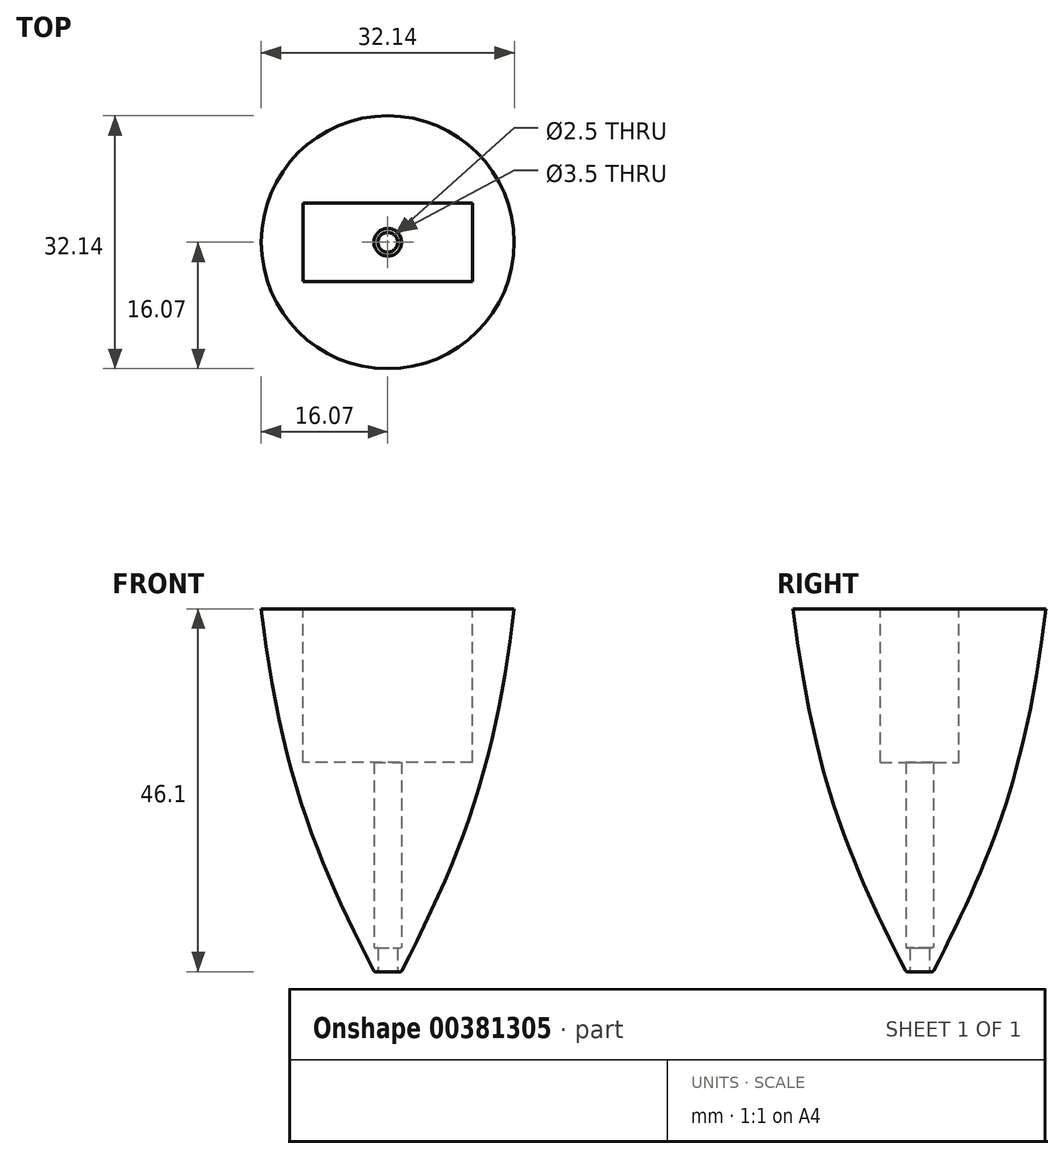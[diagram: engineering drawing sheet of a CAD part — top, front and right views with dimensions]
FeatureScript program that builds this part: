
annotation { "Feature Type Name" : "Feature", "Feature Type Description" : "" }
export const myFeature = defineFeature(function(context is Context, id is Id, definition is map)
    precondition{}
    {
        {
            var Q0;
            Q0=qCreatedBy(makeId("Front.planeOp"),FACE);
            var sketch = newSketch(context, id + "F0", { "sketchPlane" : qUnion([Q0])});
            skLineSegment(sketch, "E0.bottom", {"start": v(10.75, -19.5) * mm, "end": v(-10.75, -19.5) * mm});
            skLineSegment(sketch, "E0.top", {"start": v(10.75, 44.5) * mm, "end": v(9, 44.5) * mm});
            skLineSegment(sketch, "E0.left", {"start": v(10.75, -19.5) * mm, "end": v(10.75, 44.5) * mm});
            skLineSegment(sketch, "E0.right", {"start": v(-10.75, -19.5) * mm, "end": v(-10.75, 44.5) * mm});
            skPoint(sketch, "E0.middle", {"position": v(0, 12.5) * mm});
            skLineSegment(sketch, "E1", {"start": v(-10.75, 0) * mm, "end": v(10.75, 0) * mm, "construction": true});
            skLineSegment(sketch, "E2.top", {"start": v(9, 50.5) * mm, "end": v(-9, 50.5) * mm});
            skLineSegment(sketch, "E2.left", {"start": v(9, 44.5) * mm, "end": v(9, 50.5) * mm});
            skLineSegment(sketch, "E2.right", {"start": v(-9, 44.5) * mm, "end": v(-9, 50.5) * mm});
            skPoint(sketch, "E2.middle", {"position": v(0, 47.5) * mm});
            skPoint(sketch, "E2.middle.positionSnap0", {"position": v(0, 44.5) * mm});
            skPoint(sketch, "E2.centerSnap0", {"position": v(0, 44.5) * mm});
            skLineSegment(sketch, "E3.trimOffspring", {"start": v(-9, 44.5) * mm, "end": v(-10.75, 44.5) * mm});
            skSolve(sketch);
        }
        {
            var Q0;
            Q0=qCreatedBy(makeId("Front.planeOp"),FACE);
            var sketch = newSketch(context, id + "F1", { "sketchPlane" : qUnion([Q0])});
            skLineSegment(sketch, "E4", {"start": v(0, 0) * mm, "end": v(0, 25) * mm, "construction": true});
            skLineSegment(sketch, "E5", {"start": v(-17.5, 25) * mm, "end": v(17.5, 25) * mm, "construction": true});
            skLineSegment(sketch, "E6", {"start": v(-15, 47) * mm, "end": v(-2, 47) * mm, "construction": true});
            skPoint(sketch, "E7", {"position": v(0, 47) * mm});
            skPoint(sketch, "E8", {"position": v(0, -19.5) * mm});
            skLineSegment(sketch, "E9", {"start": v(-12.5, -19.5) * mm, "end": v(-1.25, -19.5) * mm, "construction": true});
            skLineSegment(sketch, "E10", {"start": v(0, -19.5) * mm, "end": v(0, -49.5) * mm, "construction": true});
            skLineSegment(sketch, "E11", {"start": v(0, 47) * mm, "end": v(0, 62) * mm, "construction": true});
            skLineSegment(sketch, "E12", {"start": v(-10, 62) * mm, "end": v(-2, 62) * mm});
            skFitSpline(sketch, "E13", {"points": [v(-10, 62) * mm, v(-15, 47) * mm, v(-17.5, 25) * mm, v(-12.5, -19.5) * mm, v(0, -49.5) * mm], "startDerivative": vector(-28.9, -76.62) * mm, "endDerivative": vector(51.56, -101.04) * mm});
            skLineSegment(sketch, "E14.0", {"start": v(-2, 50) * mm, "end": v(-2, 62) * mm});
            skPoint(sketch, "E15.orphan", {"position": v(10, 62) * mm});
            skLineSegment(sketch, "E16.0", {"start": v(-1.25, -43.05) * mm, "end": v(-1.25, -47.05) * mm});
            skLineSegment(sketch, "E17", {"start": v(0, 47) * mm, "end": v(-2, 47) * mm});
            skLineSegment(sketch, "E18", {"start": v(0, 50) * mm, "end": v(-2, 50) * mm});
            skLineSegment(sketch, "E19.trimOffspring", {"start": v(0, 47) * mm, "end": v(15, 47) * mm, "construction": true});
            skLineSegment(sketch, "E20.trimOffspring", {"start": v(0, -19.5) * mm, "end": v(12.5, -19.5) * mm, "construction": true});
            skLineSegment(sketch, "E21", {"start": v(0, 50) * mm, "end": v(0, -19.5) * mm});
            skLineSegment(sketch, "E22", {"start": v(0, -19.5) * mm, "end": v(-1.75, -19.5) * mm});
            skLineSegment(sketch, "E23", {"start": v(-1.75, -19.5) * mm, "end": v(-1.75, -43.05) * mm});
            skLineSegment(sketch, "E24", {"start": v(-1.25, -43.05) * mm, "end": v(-1.75, -43.05) * mm});
            skSolve(sketch);
        }
        {
            var Q0;
            Q0=makeQuery(id+"F1.imprint","IMPRINT",FACE,{"disambiguationData":[TD([[makeQuery(id+"F1.imprint","IMPRINT",EDGE,{"derivedFrom":sQuery(id+"F1.wireOp",EDGE,"E12")}),-1.0]])]});
            var Q1;
            Q1=sQuery(id+"F1.wireOp",EDGE,"E11");
            revolve(context, id + "F2", {"entities" : qUnion([Q0]), "axis" : qUnion([Q1]), "revolveType" : RevolveType.FULL});
        }
        {
            var Q0;
            Q0=qSketchRegion(id+"F0",true);
            extrude(context, id + "F3", {"entities" : qUnion([Q0]), "operationType" : NewBodyOperationType.REMOVE, "endBound" : BoundingType.SYMMETRIC, "depth" : 10 * mm});
        }
        {
            var Q0;
            Q0=makeQuery(id+"F2.opRevolve","SWEPT_FACE",FACE,{"disambiguationData":[OSD([sQuery(id+"F1.wireOp",EDGE,"E12")])]});
            var sketch = newSketch(context, id + "F4", { "sketchPlane" : qUnion([Q0])});
            skCircle(sketch, "E25.cCircle", {"center": v(0, 0) * mm, "radius": 2 * mm, "construction": true});
            skLineSegment(sketch, "E25.0", {"start": v(2.3, 0.1) * mm, "end": v(1.24, -1.95) * mm});
            skLineSegment(sketch, "E25.1", {"start": v(1.24, -1.95) * mm, "end": v(-1.06, -2.05) * mm});
            skLineSegment(sketch, "E25.2", {"start": v(-1.06, -2.05) * mm, "end": v(-2.3, -0.1) * mm});
            skLineSegment(sketch, "E25.3", {"start": v(-2.3, -0.1) * mm, "end": v(-1.24, 1.95) * mm});
            skLineSegment(sketch, "E25.4", {"start": v(-1.24, 1.95) * mm, "end": v(1.06, 2.05) * mm});
            skLineSegment(sketch, "E25.5", {"start": v(1.06, 2.05) * mm, "end": v(2.3, 0.1) * mm});
            skPoint(sketch, "E25.0.midPoint", {"position": v(1.77, -0.92) * mm});
            skSolve(sketch);
        }
        {
            var Q0;
            Q0=qSketchRegion(id+"F4",true);
            extrude(context, id + "F5", {"entities" : qUnion([Q0]), "operationType" : NewBodyOperationType.REMOVE, "oppositeDirection" : true, "depth" : 15 * mm});
        }
        {
            var Q0;
            Q0=qCreatedBy(makeId("Right.planeOp"),FACE);
            var sketch = newSketch(context, id + "F6", { "sketchPlane" : qUnion([Q0])});
            skLineSegment(sketch, "E26.bottom", {"start": v(0.1, 47) * mm, "end": v(-1.9, 47) * mm});
            skLineSegment(sketch, "E26.top", {"start": v(0.1, 50) * mm, "end": v(-1.9, 50) * mm});
            skLineSegment(sketch, "E26.left", {"start": v(0.1, 47) * mm, "end": v(0.1, 50) * mm});
            skLineSegment(sketch, "E26.right", {"start": v(-1.9, 47) * mm, "end": v(-1.9, 50) * mm});
            skPoint(sketch, "E26.middle", {"position": v(0, 48) * mm});
            skSolve(sketch);
        }
        {
            var Q0;
            Q0=qSketchRegion(id+"F6",true);
            extrude(context, id + "F7", {"entities" : qUnion([Q0]), "operationType" : NewBodyOperationType.REMOVE, "endBound" : BoundingType.SYMMETRIC, "oppositeDirection" : true, "depth" : 41 * mm});
        }
        {
            var Q0;
            Q0=qCreatedBy(makeId("Front.planeOp"),FACE);
            var sketch = newSketch(context, id + "F8", { "sketchPlane" : qUnion([Q0])});
            skLineSegment(sketch, "E27.bottom", {"start": v(1.5, 41) * mm, "end": v(-1.5, 41) * mm});
            skLineSegment(sketch, "E27.top", {"start": v(1.5, 42) * mm, "end": v(-1.5, 42) * mm});
            skLineSegment(sketch, "E27.left", {"start": v(1.5, 41) * mm, "end": v(1.5, 42) * mm});
            skLineSegment(sketch, "E27.right", {"start": v(-1.5, 41) * mm, "end": v(-1.5, 42) * mm});
            skPoint(sketch, "E27.middle", {"position": v(0, 41.5) * mm});
            skSolve(sketch);
        }
        {
            var Q0;
            Q0=qSketchRegion(id+"F8",true);
            extrude(context, id + "F9", {"entities" : qUnion([Q0]), "operationType" : NewBodyOperationType.REMOVE, "endBound" : BoundingType.THROUGH_ALL, "depth" : 25 * mm});
        }
        {
            var Q0;
            Q0=makeQuery(id+"F2.opRevolve","SWEPT_EDGE",EDGE,{"disambiguationData":[OSD([sQuery(id+"F1.wireOp",EDGE,"E13"),sQuery(id+"F1.wireOp",EDGE,"E16.0")])]});
            fillet(context, id + "F10", {"entities" : qUnion([Q0]), "radius" : 0.3 * mm, "tangentPropagation" : true, "allowEdgeOverflow" : false});
        }
        {
            var Q0;
            Q0=makeQuery(id+"F2.opRevolve","SWEPT_EDGE",EDGE,{"disambiguationData":[OSD([sQuery(id+"F1.wireOp",EDGE,"E16.0"),sQuery(id+"F1.wireOp",EDGE,"E24")])]});
            fillet(context, id + "F11", {"entities" : qUnion([Q0]), "radius" : 0.1 * mm, "tangentPropagation" : true, "allowEdgeOverflow" : false});
        }
        {
            var Q0;
            Q0=makeQuery(id+"F2.opRevolve","SWEPT_EDGE",EDGE,{"disambiguationData":[OSD([sQuery(id+"F1.wireOp",EDGE,"E23"),sQuery(id+"F1.wireOp",EDGE,"E24")])]});
            fillet(context, id + "F12", {"entities" : qUnion([Q0]), "radius" : 0.1 * mm, "tangentPropagation" : true, "allowEdgeOverflow" : false});
        }
        {
            var Q0;
            Q0=qCreatedBy(makeId("Top.planeOp"),FACE);
            var sketch = newSketch(context, id + "F13", { "sketchPlane" : qUnion([Q0])});
            skLineSegment(sketch, "E28.bottom", {"start": v(50, -50) * mm, "end": v(-50, -50) * mm});
            skLineSegment(sketch, "E28.top", {"start": v(50, 50) * mm, "end": v(-50, 50) * mm});
            skLineSegment(sketch, "E28.left", {"start": v(50, -50) * mm, "end": v(50, 50) * mm});
            skLineSegment(sketch, "E28.right", {"start": v(-50, -50) * mm, "end": v(-50, 50) * mm});
            skPoint(sketch, "E28.middle", {"position": v(0, 0) * mm});
            skSolve(sketch);
        }
        {
            var Q0;
            Q0 = qSketchRegion(id + "F13", true);
            extrude(context, id + "F14", {"entities" : qUnion([Q0]), "operationType" : NewBodyOperationType.REMOVE, "endBound" : BoundingType.THROUGH_ALL, "depth" : 25 * mm});
        }
    });
